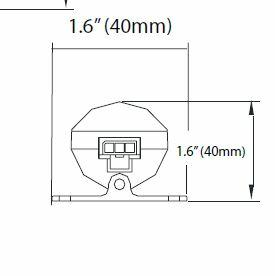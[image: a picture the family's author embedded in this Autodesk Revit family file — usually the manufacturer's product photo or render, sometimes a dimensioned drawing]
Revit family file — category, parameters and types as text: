
# Revit family: Lighting-Surface-Acclaim-Flex Tube HO SC
name_source: partatom
category: Lighting Fixtures
units: mm (PartAtom-declared; Revit-internal decimal feet)

## family parameters
Cut with Voids When Loaded = No
Host = Face
Light Source = Yes
Part Type = Normal
Room Calculation Point = No
Round Connector Dimension = Use Diameter
Shared = No

## types (1)
- Lighting-Surface-Acclaim-Flex Tube HO SC
    Apparent Load = 0 VA
    Color Filter = 16777215
    Default Elevation = 48 "
    Description = Linear LED Strip
    Dimming Lamp Color Temperature Shift = <None>
    Emit from Line Length = 24 "
    Height = 0.88 "
    Housing Finish = Aluminum
    Lamp = LED
    Length = 24 "
    Manufacturer = Acclaim Lighting
    Model = Flex Tube HO SC
    Number of Poles = 1
    Photometric Web File = Load File
    Power Factor = 1
    Tilt Angle = 90.00°
    URL = http://www.acclaimlighting.com
    Voltage = 0 V
    Width = 0.89 "

## geometry (parser evidence)
native form markers: Blend x13, Sweep x3
no freeform markers — native parametric forms only
